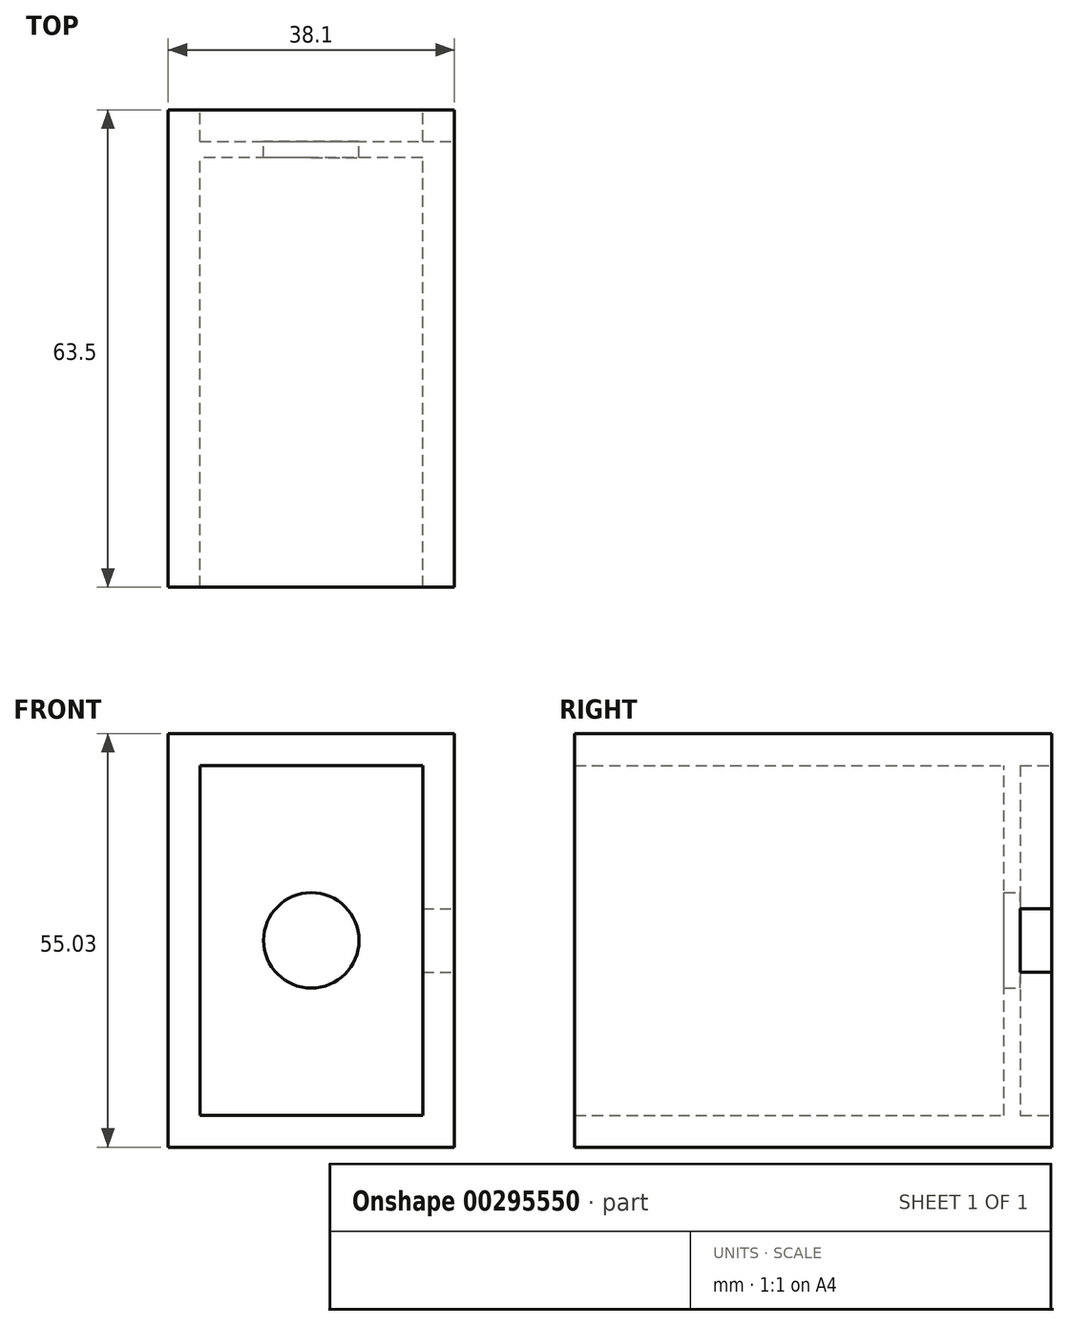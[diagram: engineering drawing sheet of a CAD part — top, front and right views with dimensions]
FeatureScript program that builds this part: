
annotation { "Feature Type Name" : "Feature", "Feature Type Description" : "" }
export const myFeature = defineFeature(function(context is Context, id is Id, definition is map)
    precondition{}
    {
        {
            var Q0;
            Q0=qCreatedBy(makeId("Front.planeOp"),FACE);
            var sketch = newSketch(context, id + "F0", { "sketchPlane" : qUnion([Q0])});
            skLineSegment(sketch, "E0", {"start": v(69.85, 0) * mm, "end": v(69.85, -55.03) * mm});
            skLineSegment(sketch, "E1.bottom", {"start": v(69.85, -55.03) * mm, "end": v(31.75, -55.03) * mm});
            skLineSegment(sketch, "E1.top", {"start": v(69.85, 0) * mm, "end": v(31.75, 0) * mm});
            skLineSegment(sketch, "E1.left", {"start": v(69.85, -55.03) * mm, "end": v(69.85, 0) * mm});
            skLineSegment(sketch, "E1.right", {"start": v(31.75, -55.03) * mm, "end": v(31.75, 0) * mm});
            skLineSegment(sketch, "E2", {"start": v(69.85, 0) * mm, "end": v(69.85, 2.96) * mm});
            skPoint(sketch, "E3.visualSharp", {"position": v(69.85, 4.23) * mm});
            skArc(sketch, "E3.filletArc", {"start": v(69.85, 2.96) * mm, "mid": v(69.48, 3.86) * mm, "end": v(68.58, 4.23) * mm});
            skLineSegment(sketch, "E4", {"start": v(69.85, 0) * mm, "end": v(69.85, -4.23) * mm});
            skLineSegment(sketch, "E5", {"start": v(69.85, -4.23) * mm, "end": v(65.62, -4.23) * mm});
            skLineSegment(sketch, "E6", {"start": v(31.75, -55.03) * mm, "end": v(31.75, -50.8) * mm});
            skLineSegment(sketch, "E7", {"start": v(31.75, -50.8) * mm, "end": v(35.98, -50.8) * mm});
            skLineSegment(sketch, "E8.bottom", {"start": v(35.98, -50.8) * mm, "end": v(65.62, -50.8) * mm});
            skLineSegment(sketch, "E8.top", {"start": v(35.98, -4.23) * mm, "end": v(65.62, -4.23) * mm});
            skLineSegment(sketch, "E8.left", {"start": v(35.98, -50.8) * mm, "end": v(35.98, -4.23) * mm});
            skLineSegment(sketch, "E8.right", {"start": v(65.62, -50.8) * mm, "end": v(65.62, -4.23) * mm});
            skSolve(sketch);
        }
        {
            var Q0;
            Q0 = qSketchRegion(id + "F0", true);
            extrude(context, id + "F1", {"entities" : qUnion([Q0]), "depth" : 63.5 * mm});
        }
        {
            var Q0;
            Q0=qCreatedBy(makeId("Front.planeOp"),FACE);
            var sketch = newSketch(context, id + "F2", { "sketchPlane" : qUnion([Q0])});
            skLineSegment(sketch, "E9", {"start": v(0, 0) * mm, "end": v(35.98, 0) * mm});
            skLineSegment(sketch, "E10", {"start": v(35.98, 0) * mm, "end": v(35.98, -4.23) * mm});
            skLineSegment(sketch, "E11", {"start": v(69.85, -55.03) * mm, "end": v(69.85, -50.8) * mm});
            skLineSegment(sketch, "E12", {"start": v(69.85, -50.8) * mm, "end": v(65.62, -50.8) * mm});
            skLineSegment(sketch, "E13.bottom", {"start": v(65.62, -50.8) * mm, "end": v(35.98, -50.8) * mm});
            skLineSegment(sketch, "E13.top", {"start": v(65.62, -4.23) * mm, "end": v(35.98, -4.23) * mm});
            skLineSegment(sketch, "E13.left", {"start": v(65.62, -50.8) * mm, "end": v(65.62, -4.23) * mm});
            skLineSegment(sketch, "E13.right", {"start": v(35.98, -50.8) * mm, "end": v(35.98, -4.23) * mm});
            skSolve(sketch);
        }
        {
            var Q0;
            Q0 = qSketchRegion(id + "F2", true);
            extrude(context, id + "F3", {"entities" : qUnion([Q0]), "operationType" : NewBodyOperationType.ADD, "depth" : 6.35 * mm});
        }
        {
            var Q0;
            Q0=qCreatedBy(makeId("Front.planeOp"),FACE);
            var sketch = newSketch(context, id + "F4", { "sketchPlane" : qUnion([Q0])});
            skLineSegment(sketch, "E14", {"start": v(0, 0) * mm, "end": v(35.98, 0) * mm});
            skLineSegment(sketch, "E15", {"start": v(35.98, 0) * mm, "end": v(35.98, -4.23) * mm});
            skLineSegment(sketch, "E16", {"start": v(65.62, -4.23) * mm, "end": v(65.62, -55.03) * mm});
            skLineSegment(sketch, "E17", {"start": v(65.62, -55.03) * mm, "end": v(65.62, -50.8) * mm});
            skLineSegment(sketch, "E18.bottom", {"start": v(35.98, -4.23) * mm, "end": v(65.62, -4.23) * mm});
            skLineSegment(sketch, "E18.top", {"start": v(35.98, -50.8) * mm, "end": v(65.62, -50.8) * mm});
            skLineSegment(sketch, "E18.left", {"start": v(35.98, -4.23) * mm, "end": v(35.98, -50.8) * mm});
            skLineSegment(sketch, "E18.right", {"start": v(65.62, -4.23) * mm, "end": v(65.62, -50.8) * mm});
            skSolve(sketch);
        }
        {
            var Q0;
            Q0 = qSketchRegion(id + "F4", true);
            extrude(context, id + "F5", {"entities" : qUnion([Q0]), "operationType" : NewBodyOperationType.REMOVE, "depth" : 4.2 * mm});
        }
        {
            var Q0;
            Q0=makeQuery(id+"F3.boolean.opBoolean","MERGE",FACE,{"derivedFrom":[makeQuery(id+"F1.opExtrude","CAP_FACE",FACE,{"disambiguationData":[OSD([sQuery(id+"F0.wireOp",EDGE,"E1.bottom"),sQuery(id+"F0.wireOp",EDGE,"E1.top"),sQuery(id+"F0.wireOp",EDGE,"E1.left"),sQuery(id+"F0.wireOp",EDGE,"E1.right"),sQuery(id+"F0.wireOp",EDGE,"E4"),sQuery(id+"F0.wireOp",EDGE,"E6"),sQuery(id+"F0.wireOp",EDGE,"E8.bottom"),sQuery(id+"F0.wireOp",EDGE,"E8.top"),sQuery(id+"F0.wireOp",EDGE,"E8.left"),sQuery(id+"F0.wireOp",EDGE,"E8.right")])],"isStart":true}),makeQuery(id+"F3.opExtrude","CAP_FACE",FACE,{"disambiguationData":[OSD([sQuery(id+"F2.wireOp",EDGE,"E13.bottom"),sQuery(id+"F2.wireOp",EDGE,"E13.top"),sQuery(id+"F2.wireOp",EDGE,"E13.left"),sQuery(id+"F2.wireOp",EDGE,"E13.right")])],"isStart":true})]});
            var sketch = newSketch(context, id + "F6", { "sketchPlane" : qUnion([Q0])});
            skLineSegment(sketch, "E19", {"start": v(-69.85, 0) * mm, "end": v(-69.85, -27.52) * mm});
            skLineSegment(sketch, "E20", {"start": v(-69.85, -27.52) * mm, "end": v(-67.73, -27.52) * mm});
            skPoint(sketch, "E20.endSnap0", {"position": v(-65.62, -27.52) * mm});
            skLineSegment(sketch, "E21.bottom", {"start": v(-65.62, -23.28) * mm, "end": v(-69.85, -23.28) * mm});
            skLineSegment(sketch, "E21.top", {"start": v(-65.62, -31.75) * mm, "end": v(-69.85, -31.75) * mm});
            skLineSegment(sketch, "E21.left", {"start": v(-65.62, -23.28) * mm, "end": v(-65.62, -31.75) * mm});
            skLineSegment(sketch, "E21.right", {"start": v(-69.85, -23.28) * mm, "end": v(-69.85, -31.75) * mm});
            skPoint(sketch, "E21.middle", {"position": v(-67.73, -27.52) * mm});
            skSolve(sketch);
        }
        {
            var Q0;
            Q0 = qSketchRegion(id + "F6", true);
            extrude(context, id + "F7", {"entities" : qUnion([Q0]), "operationType" : NewBodyOperationType.REMOVE, "oppositeDirection" : true, "depth" : 4.2 * mm});
        }
        {
            var Q0;
            Q0=makeQuery(id+"F7.boolean.opBoolean","MERGE",FACE,{"derivedFrom":[makeQuery(id+"F5.boolean.opBoolean","COPY",FACE,{"derivedFrom":makeQuery(id+"F5.opExtrude","CAP_FACE",FACE,{"disambiguationData":[OSD([sQuery(id+"F4.wireOp",EDGE,"E18.bottom"),sQuery(id+"F4.wireOp",EDGE,"E18.top"),sQuery(id+"F4.wireOp",EDGE,"E18.left"),sQuery(id+"F4.wireOp",EDGE,"E18.right")])],"isStart":false})}),makeQuery(id+"F7.opExtrude","CAP_FACE",FACE,{"disambiguationData":[OSD([sQuery(id+"F6.wireOp",EDGE,"E21.bottom"),sQuery(id+"F6.wireOp",EDGE,"E21.top"),sQuery(id+"F6.wireOp",EDGE,"E21.left"),sQuery(id+"F6.wireOp",EDGE,"E21.right")])],"isStart":false})]});
            var sketch = newSketch(context, id + "F8", { "sketchPlane" : qUnion([Q0])});
            skLineSegment(sketch, "E22", {"start": v(-65.62, -4.23) * mm, "end": v(-50.8, -4.23) * mm});
            skLineSegment(sketch, "E23", {"start": v(-50.8, -4.23) * mm, "end": v(-50.8, -27.52) * mm});
            skCircle(sketch, "E24", {"center": v(-50.8, -27.52) * mm, "radius": 6.35 * mm});
            skSolve(sketch);
        }
        {
            var Q0;
            Q0 = qSketchRegion(id + "F8", true);
            extrude(context, id + "F9", {"entities" : qUnion([Q0]), "operationType" : NewBodyOperationType.REMOVE, "endBound" : BoundingType.THROUGH_ALL, "oppositeDirection" : true, "depth" : 25.4 * mm});
        }
    });
